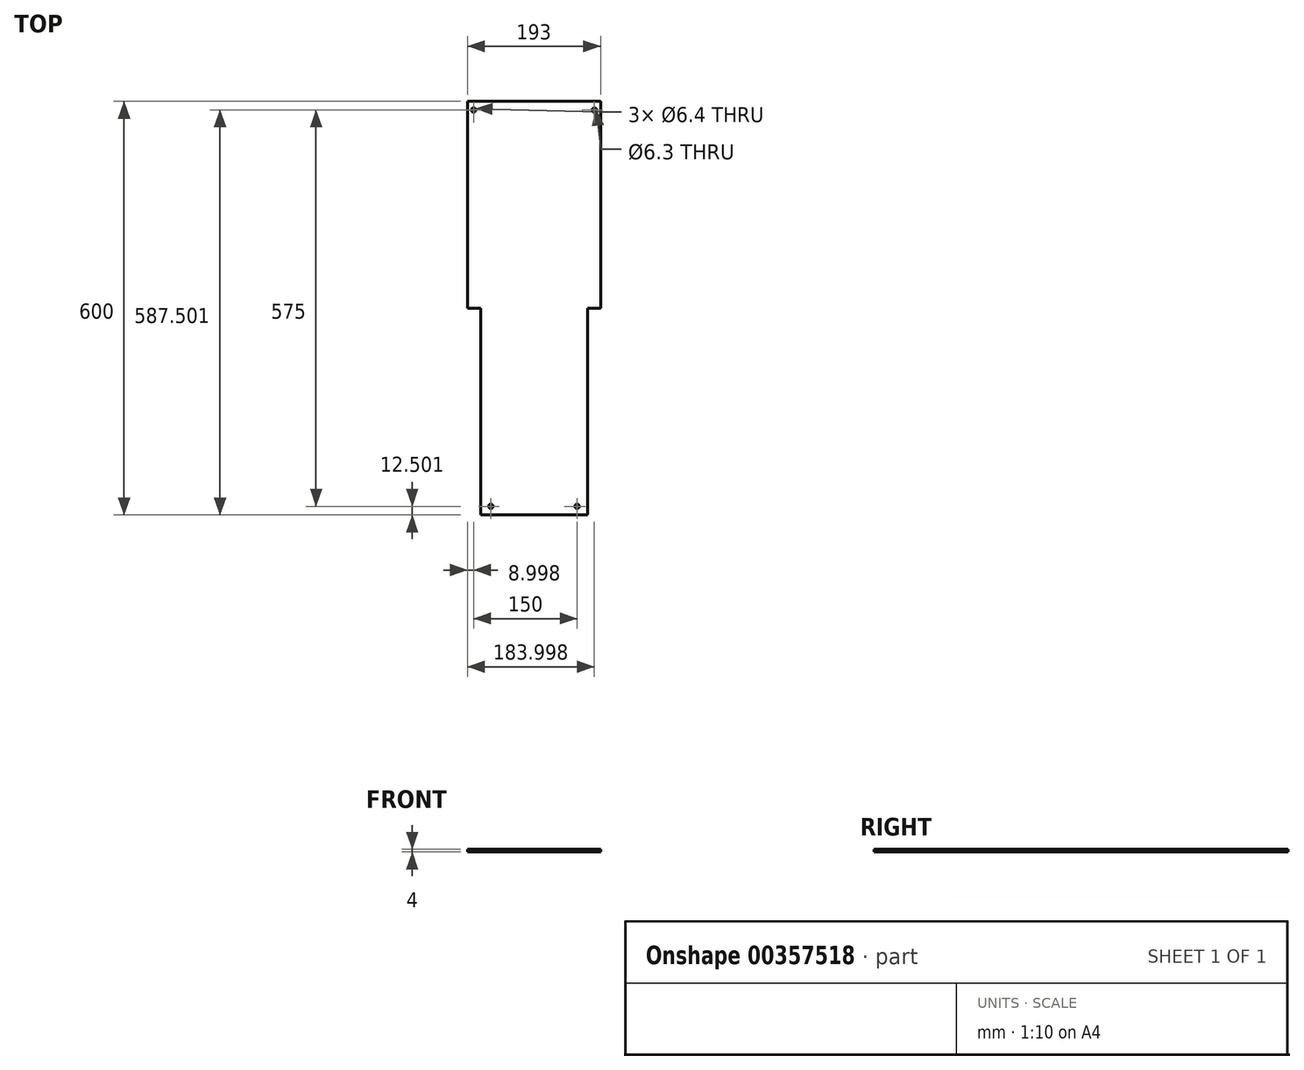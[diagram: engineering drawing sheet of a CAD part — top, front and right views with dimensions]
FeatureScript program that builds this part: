
annotation { "Feature Type Name" : "Feature", "Feature Type Description" : "" }
export const myFeature = defineFeature(function(context is Context, id is Id, definition is map)
    precondition{}
    {
        {
            var Q0;
            Q0=qCreatedBy(makeId("Top.planeOp"),FACE);
            var sketch = newSketch(context, id + "F0", { "sketchPlane" : qUnion([Q0])});
            skLineSegment(sketch, "E0", {"start": v(-235.7, 253.21) * mm, "end": v(-235.7, -46.79) * mm});
            skLineSegment(sketch, "E1", {"start": v(-235.7, -46.79) * mm, "end": v(-216.7, -46.79) * mm});
            skLineSegment(sketch, "E2", {"start": v(-216.7, -46.79) * mm, "end": v(-216.7, -346.79) * mm});
            skLineSegment(sketch, "E3", {"start": v(-216.7, -346.79) * mm, "end": v(-61.7, -346.79) * mm});
            skLineSegment(sketch, "E4", {"start": v(-61.7, -346.79) * mm, "end": v(-61.7, -46.79) * mm});
            skLineSegment(sketch, "E5", {"start": v(-61.7, -46.79) * mm, "end": v(-42.7, -46.79) * mm});
            skLineSegment(sketch, "E6", {"start": v(-42.7, -46.79) * mm, "end": v(-42.7, 253.21) * mm});
            skLineSegment(sketch, "E7", {"start": v(-42.7, 253.21) * mm, "end": v(-235.7, 253.21) * mm});
            skCircle(sketch, "E8", {"center": v(-226.7, 240.71) * mm, "radius": 3.2 * mm});
            skCircle(sketch, "E9", {"center": v(-201.7, -334.29) * mm, "radius": 3.2 * mm});
            skCircle(sketch, "E10.MirrorC", {"center": v(-51.7, 240.71) * mm, "radius": 3.15 * mm});
            skCircle(sketch, "E11.MirrorC", {"center": v(-76.7, -334.29) * mm, "radius": 3.2 * mm});
            skLineSegment(sketch, "E12", {"start": v(-139.2, 253.21) * mm, "end": v(-139.2, -346.79) * mm});
            skSolve(sketch);
        }
        {
            var Q0;
            Q0 = qSketchRegion(id + "F0", true);
            extrude(context, id + "F1", {"entities" : qUnion([Q0]), "depth" : 4 * mm});
        }
    });
